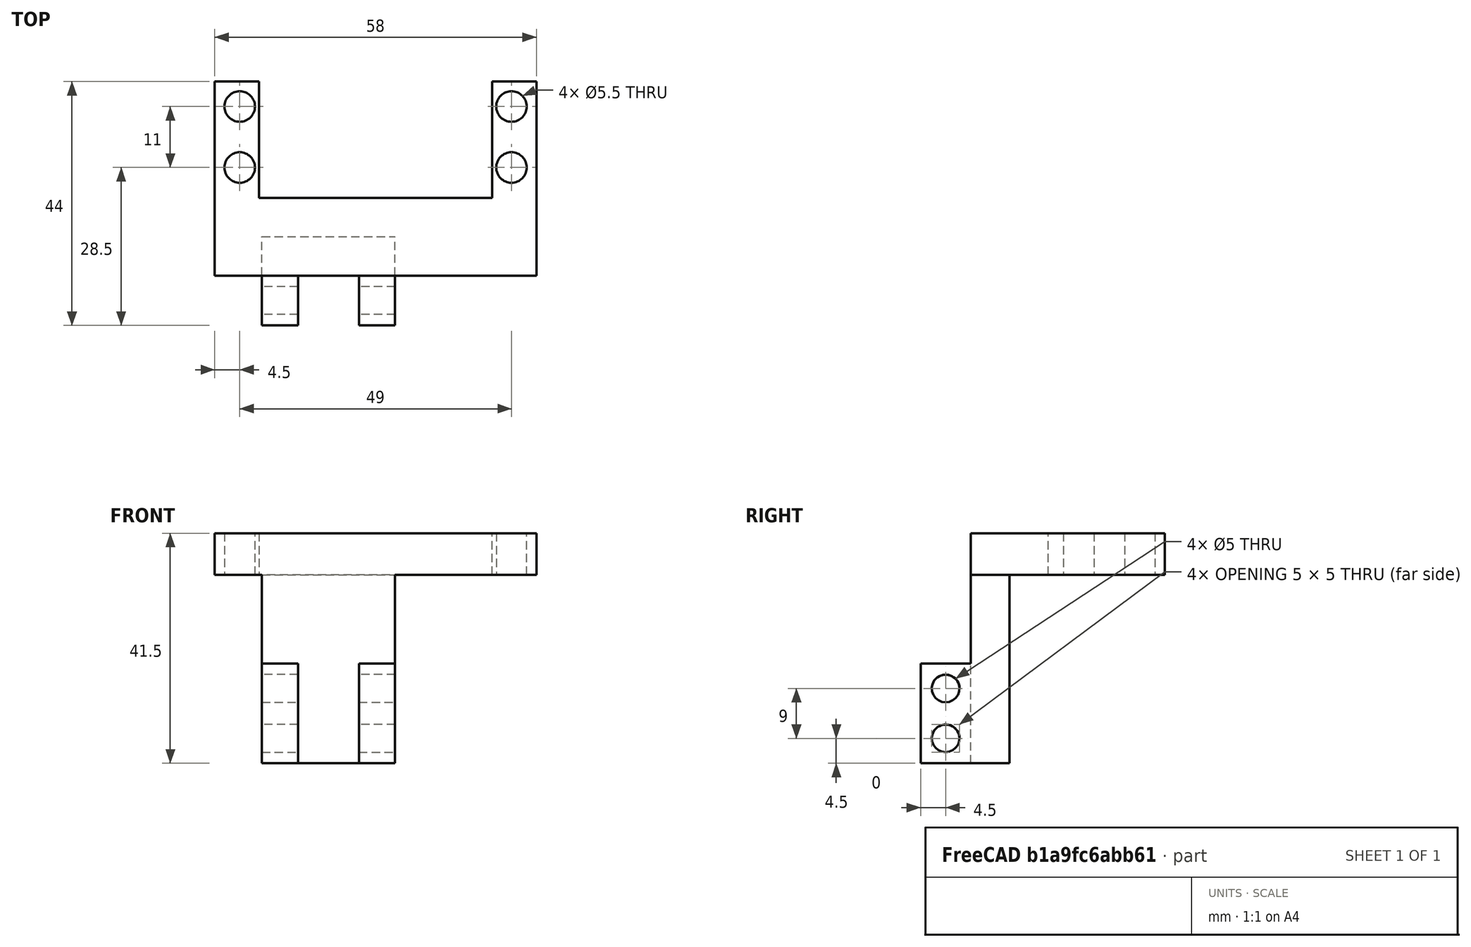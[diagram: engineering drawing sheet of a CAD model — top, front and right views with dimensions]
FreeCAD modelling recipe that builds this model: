
FCSTD DOCUMENT  (FreeCAD 0.21R33668 +26 (Git))
Label: Arm Holder
License: All rights reserved
LicenseURL: https://en.wikipedia.org/wiki/All_rights_reserved
objects: Part::Cylinder×6, Part::Box×5, Part::MultiFuse×5, Part::Cut×2
note: 18 computed .brp shape members not serialized (recipe doc carries the construction recipe); baked Part::Feature solids carry a one-line shape summary decoded from their .brp

FEATURE [Part::Box] Box  label="Servo Mold"
  AttacherType = Attacher::AttachEngine3D
  Height = 18
  Length = 42
  Placement = pos=(-1,-1,0) rot=(0,0,1;0rad)
  Width = 22
FEATURE [Part::Cylinder] Cylinder  label="Hole001"
  Angle = 360
  AttacherType = Attacher::AttachEngine3D
  FirstAngle = 0
  Height = 18
  Placement = pos=(-4.5,4.5,0) rot=(0,0,1;0rad)
  Radius = 2.75
  SecondAngle = 0
FEATURE [Part::Cylinder] Cylinder001  label="Hole002"
  Angle = 360
  AttacherType = Attacher::AttachEngine3D
  FirstAngle = 0
  Height = 18
  Placement = pos=(-4.5,15.5,0) rot=(0,0,1;0rad)
  Radius = 2.75
  SecondAngle = 0
FEATURE [Part::Cylinder] Cylinder002  label="Hole003"
  Angle = 360
  AttacherType = Attacher::AttachEngine3D
  FirstAngle = 0
  Height = 18
  Placement = pos=(44.5,4.5,0) rot=(0,0,1;0rad)
  Radius = 2.75
  SecondAngle = 0
FEATURE [Part::Cylinder] Cylinder003  label="Hole004"
  Angle = 360
  AttacherType = Attacher::AttachEngine3D
  FirstAngle = 0
  Height = 18
  Placement = pos=(44.5,15.5,0) rot=(0,0,1;0rad)
  Radius = 2.75
  SecondAngle = 0
FEATURE [Part::Box] Box002  label="Servo Holder"
  AttacherType = Attacher::AttachEngine3D
  Height = 7.5
  Length = 58
  Placement = pos=(-9,-15,10.5) rot=(0,0,1;0rad)
  Width = 35
FEATURE [Part::MultiFuse] Fusion  label="Servo Holes"
  Shapes = -> [Cylinder,Cylinder001,Cylinder002,Cylinder003]
FEATURE [Part::MultiFuse] Fusion001  label="Servo Object"
  Shapes = -> [Fusion,Box]
FEATURE [Part::Cut] Cut  label="Servo Mount"
  Base = -> Box002
  Tool = -> Fusion001
FEATURE [Part::Box] Box003  label="Cube"
  AttacherType = Attacher::AttachEngine3D
  Height = 34
  Length = 24
  Placement = pos=(-0.5,-15,-23.5) rot=(0,0,1;0rad)
  Width = 7
FEATURE [Part::Box] Box004  label="Cube001"
  AttacherType = Attacher::AttachEngine3D
  Height = 18
  Length = 6.5
  Placement = pos=(-0.5,-24,-23.5) rot=(0,0,1;0rad)
  Width = 9
FEATURE [Part::Box] Box005  label="Cube002"
  AttacherType = Attacher::AttachEngine3D
  Height = 18
  Length = 6.5
  Placement = pos=(17,-24,-23.5) rot=(0,0,1;0rad)
  Width = 9
FEATURE [Part::MultiFuse] Fusion002  label="Module Holder"
  Shapes = -> [Box005,Box004,Box003]
FEATURE [Part::Cylinder] Cylinder004  label="Cylinder"
  Angle = 360
  AttacherType = Attacher::AttachEngine3D
  FirstAngle = 0
  Height = 27
  Placement = pos=(-2,-19.5,-19) rot=(0,1,0;1.5708rad)
  Radius = 2.5
  SecondAngle = 0
FEATURE [Part::Cylinder] Cylinder005
  Angle = 360
  AttacherType = Attacher::AttachEngine3D
  FirstAngle = 0
  Height = 27
  Placement = pos=(-2,-19.5,-10) rot=(0,1,0;1.5708rad)
  Radius = 2.5
  SecondAngle = 0
FEATURE [Part::MultiFuse] Fusion003
  Shapes = -> [Cylinder004,Cylinder005]
FEATURE [Part::Cut] Cut001  label="Module Hole-der"
  Base = -> Fusion002
  Tool = -> Fusion003
FEATURE [Part::MultiFuse] Fusion004  label="Complete Arm Holder"
  Shapes = -> [Cut,Cut001]
